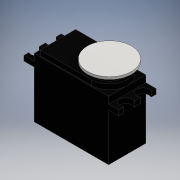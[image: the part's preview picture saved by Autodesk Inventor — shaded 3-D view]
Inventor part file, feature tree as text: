
AUTODESK INVENTOR PART (.ipt)
format: ipt  version: 2016 (Build 200138000, 138)  size: 212,992 bytes
history: native  units: mm
features: extrude x7, sketch x7, fillet x2, mirror x1
ambient origin geometry x8: Origin, YZ Plane, XZ Plane, XY Plane, X Axis, Y Axis, Z Axis, Center Point
bodies: Solid1 (feature_tree)
feature tree (17):
  extrude  "Extrusion1"  Depth=35.0mm
  extrude  "Extrusion2"  Depth=3.0mm
  fillet  "Fillet1"  Radius=0.5mm
  fillet  "Fillet2"  Radius=0.5mm
  extrude  "Extrusion3"  Depth=3.0mm TaperAngle=0.0deg
  extrude  "Extrusion4"  Depth=10.5mm
  extrude  "Extrusion5"  Depth=1.0mm TaperAngle=0.0deg
  extrude  "Extrusion6"  Depth=3.0mm TaperAngle=0.0deg
  extrude  "Extrusion7"  Depth=1.5mm TaperAngle=0.0deg
  mirror  "Mirror1"
  sketch  "Sketch1"  dims[d0=44.0mm d1=35.0mm]
  sketch  "Sketch2"  dims[d2=22.0mm d3=0.0mm d4=3.0mm d5=0.5mm d6=0.5mm]
  sketch  "Sketch3"  dims[d7=0.0mm d9=3.0mm d10=0.0mm]
  sketch  "Sketch4"  dims[d11=10.5mm d12=10.5mm]
  sketch  "Sketch5"  dims[d13=2.0mm d14=1.0mm d15=0.0mm]
  sketch  "Sketch7"  dims[d16=3.0mm d17=3.0mm d18=0.0mm]
  sketch  "Sketch8"  dims[d19=26.0mm d20=1.5mm d21=0.0mm d22=4.0mm d23=3.0mm d24=0.0mm d25=0.0mm d26=6.0mm d27=0.0mm d28=7.0mm d29=6.0mm d30=7.0mm d31=6.0mm d32=1.7mm d33=1.7mm d34=0.0mm d35=0.0mm]
